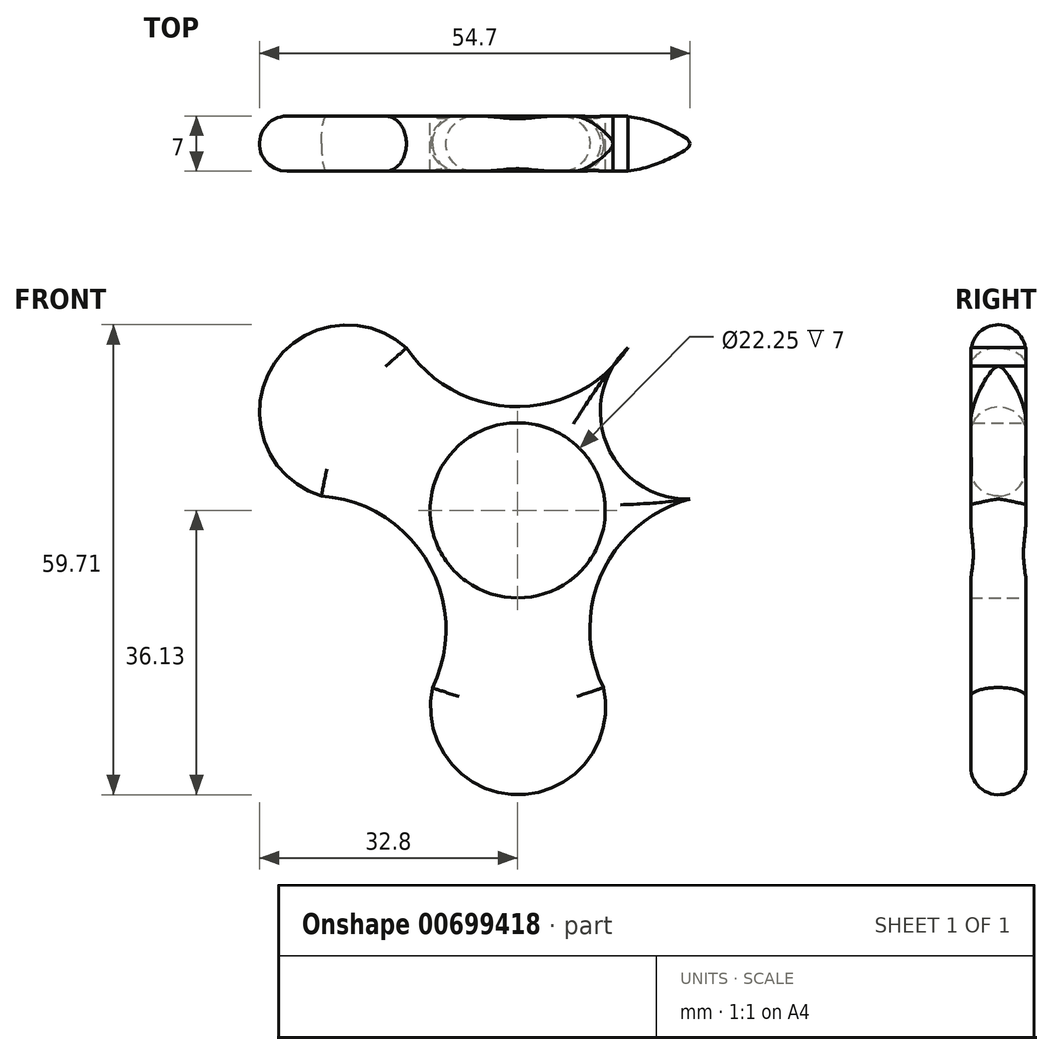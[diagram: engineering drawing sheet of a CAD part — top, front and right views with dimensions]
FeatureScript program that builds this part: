
annotation { "Feature Type Name" : "Feature", "Feature Type Description" : "" }
export const myFeature = defineFeature(function(context is Context, id is Id, definition is map)
    precondition{}
    {
        {
            var Q0;
            Q0=qCreatedBy(makeId("Front.planeOp"),FACE);
            var sketch = newSketch(context, id + "F0", { "sketchPlane" : qUnion([Q0])});
            skCircle(sketch, "E0", {"center": v(0, 0) * mm, "radius": 11.12 * mm});
            skCircle(sketch, "E1", {"center": v(0.05, -25) * mm, "radius": 11.12 * mm});
            skCircle(sketch, "E2.1.1", {"center": v(21.63, 12.54) * mm, "radius": 11.12 * mm});
            skCircle(sketch, "E2.2.1", {"center": v(-21.68, 12.46) * mm, "radius": 11.12 * mm});
            skArc(sketch, "E3", {"start": v(24.93, 1.92) * mm, "mid": v(11.42, -6.57) * mm, "end": v(10.9, -22.5) * mm});
            skArc(sketch, "E4", {"start": v(-10.8, -22.55) * mm, "mid": v(-11.4, -6.61) * mm, "end": v(-24.93, 1.82) * mm});
            skArc(sketch, "E5", {"start": v(-14.13, 20.63) * mm, "mid": v(-0.03, 13.18) * mm, "end": v(14.04, 20.68) * mm});
            skSolve(sketch);
        }
        {
            var Q0;
            {var subQ0=sQuery(id+"F0.wireOp",EDGE,"E3");var subQ1=sQuery(id+"F0.wireOp",EDGE,"E1");var subQ2=makeQuery(id+"F0.imprint","INTERSECT",VERTEX,{"disambiguationData":[OD(1.0)],"derivedFrom":[subQ1,subQ0]});Q0=makeQuery(id+"F0.imprint","IMPRINT",FACE,{"disambiguationData":[TD([[makeQuery(id+"F0.imprint","IMPRINT",EDGE,{"disambiguationData":[TD([[subQ2,-1.0]])],"derivedFrom":subQ1}),1.0]])]});}
            var Q1;
            Q1=makeQuery(id+"F0.imprint","IMPRINT",FACE,{"disambiguationData":[TD([[makeQuery(id+"F0.imprint","IMPRINT",EDGE,{"derivedFrom":sQuery(id+"F0.wireOp",EDGE,"E0")}),-1.0]])]});
            var Q2;
            {var subQ0=sQuery(id+"F0.wireOp",EDGE,"E4");var subQ1=sQuery(id+"F0.wireOp",EDGE,"E2.2.1");var subQ2=makeQuery(id+"F0.imprint","INTERSECT",VERTEX,{"disambiguationData":[OD(1.0)],"derivedFrom":[subQ1,subQ0]});Q2=makeQuery(id+"F0.imprint","IMPRINT",FACE,{"disambiguationData":[TD([[makeQuery(id+"F0.imprint","IMPRINT",EDGE,{"disambiguationData":[TD([[subQ2,-1.0]])],"derivedFrom":subQ1}),1.0]])]});}
            var Q3;
            {var subQ0=sQuery(id+"F0.wireOp",EDGE,"E5");var subQ1=sQuery(id+"F0.wireOp",EDGE,"E2.1.1");var subQ2=makeQuery(id+"F0.imprint","INTERSECT",VERTEX,{"disambiguationData":[OD(1.0)],"derivedFrom":[subQ1,subQ0]});Q3=makeQuery(id+"F0.imprint","IMPRINT",FACE,{"disambiguationData":[TD([[makeQuery(id+"F0.imprint","IMPRINT",EDGE,{"disambiguationData":[TD([[subQ2,-1.0]])],"derivedFrom":subQ1}),1.0]])]});}
            extrude(context, id + "F1", {"entities" : qUnion([Q0, Q1, Q2, Q3]), "depth" : 7 * mm, "offsetDistance" : 25 * mm});
        }
        {
            var Q0;
            Q0=makeQuery(id+"F1.opExtrude","CAP_EDGE",EDGE,{"disambiguationData":[OSD([sQuery(id+"F0.wireOp",EDGE,"E3")])],"isStart":false});
            var Q1;
            Q1=makeQuery(id+"F1.opExtrude","CAP_EDGE",EDGE,{"disambiguationData":[OSD([sQuery(id+"F0.wireOp",EDGE,"E1")])],"isStart":false});
            var Q2;
            Q2=makeQuery(id+"F1.opExtrude","CAP_EDGE",EDGE,{"disambiguationData":[OSD([sQuery(id+"F0.wireOp",EDGE,"E4")])],"isStart":false});
            var Q3;
            Q3=makeQuery(id+"F1.opExtrude","CAP_EDGE",EDGE,{"disambiguationData":[OSD([sQuery(id+"F0.wireOp",EDGE,"E2.2.1")])],"isStart":false});
            var Q4;
            Q4=makeQuery(id+"F1.opExtrude","CAP_EDGE",EDGE,{"disambiguationData":[OSD([sQuery(id+"F0.wireOp",EDGE,"E5")])],"isStart":false});
            var Q5;
            Q5=makeQuery(id+"F1.opExtrude","CAP_EDGE",EDGE,{"disambiguationData":[OSD([sQuery(id+"F0.wireOp",EDGE,"E3")])],"isStart":true});
            var Q6;
            Q6=makeQuery(id+"F1.opExtrude","CAP_EDGE",EDGE,{"disambiguationData":[OSD([sQuery(id+"F0.wireOp",EDGE,"E1")])],"isStart":true});
            var Q7;
            Q7=makeQuery(id+"F1.opExtrude","CAP_EDGE",EDGE,{"disambiguationData":[OSD([sQuery(id+"F0.wireOp",EDGE,"E4")])],"isStart":true});
            var Q8;
            Q8=makeQuery(id+"F1.opExtrude","CAP_EDGE",EDGE,{"disambiguationData":[OSD([sQuery(id+"F0.wireOp",EDGE,"E2.2.1")])],"isStart":true});
            var Q9;
            Q9=makeQuery(id+"F1.opExtrude","CAP_EDGE",EDGE,{"disambiguationData":[OSD([sQuery(id+"F0.wireOp",EDGE,"E5")])],"isStart":true});
            var Q10;
            Q10=makeQuery(id+"F1.opExtrude","CAP_EDGE",EDGE,{"disambiguationData":[OSD([sQuery(id+"F0.wireOp",EDGE,"E2.1.1")])],"isStart":true});
            var Q11;
            Q11=makeQuery(id+"F1.opExtrude","CAP_EDGE",EDGE,{"disambiguationData":[OSD([sQuery(id+"F0.wireOp",EDGE,"E2.1.1")])],"isStart":false});
            fillet(context, id + "F2", {"entities" : qUnion([Q0, Q1, Q2, Q3, Q4, Q5, Q6, Q7, Q8, Q9, Q10, Q11]), "radius" : 3.5 * mm, "tangentPropagation" : true, "allowEdgeOverflow" : false});
        }
    });
